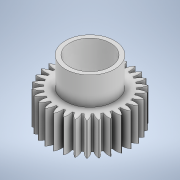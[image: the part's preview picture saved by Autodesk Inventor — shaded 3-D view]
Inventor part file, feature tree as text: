
AUTODESK INVENTOR PART (.ipt)
format: ipt  version: 2022 (Build 260153000, 153)  size: 296,448 bytes
history: native  units: mm
features: extrude x4, sketch x4, other x1, pattern_circular x1
ambient origin geometry x8: Origin, YZ Plane, XZ Plane, XY Plane, X Axis, Y Axis, Z Axis, Center Point
bodies: Body1 (feature_tree)
feature tree (10):
  other  "Bryła1"
  extrude  "Wyciągnięcie proste3"  Depth=20.0mm TaperAngle=0.0deg
  extrude  "Wyciągnięcie proste4"  Depth=30.0mm
  sketch  "Szkic3"
  sketch  "Szkic4"
  sketch  "Szkic1"
  sketch  "Szkic2"
  pattern_circular  "Szyk kołowy1"  [2 undecoded]
  extrude  "Wyciągnięcie proste1"  Depth=17.0mm TaperAngle=0.0deg
  extrude  "Wyciągnięcie proste2"  TaperAngle=0.0deg  [1 undecoded]
note: 3 required parameter values undecoded (feature->parameter linkage not recoverable at this tier; creation-order binding heuristic only, values carry confidence <= 0.55)
